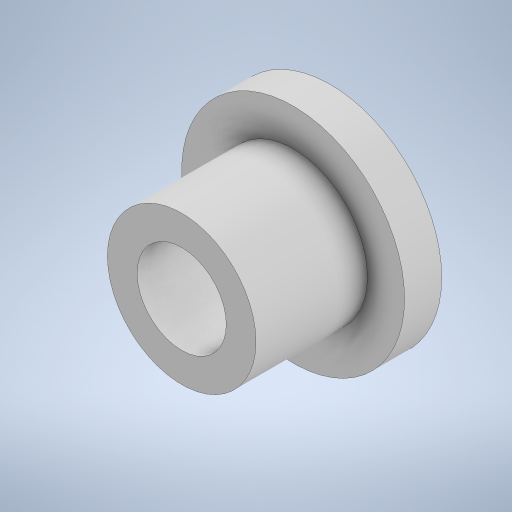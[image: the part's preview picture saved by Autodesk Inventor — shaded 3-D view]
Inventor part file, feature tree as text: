
AUTODESK INVENTOR PART (.ipt)
format: ipt  version: 2024 (Build 280153000, 153)  size: 242,688 bytes
history: native  units: mm
features: extrude x2, other x1, sketch x1
ambient origin geometry x8: Origin, YZ Plane, XZ Plane, XY Plane, X Axis, Y Axis, Z Axis, Center Point
bodies: Body1 (feature_tree)
feature tree (4):
  other  "Sólido1"
  sketch  "Boceto1"  dims[d0=30.0mm d1=20.0mm d2=12.0mm d3=5.0mm d4=0.0mm d5=15.0mm d6=0.0mm]
  extrude  "Extrusión1"  Depth=20.0mm
  extrude  "Extrusión2"  Depth=15.0mm
